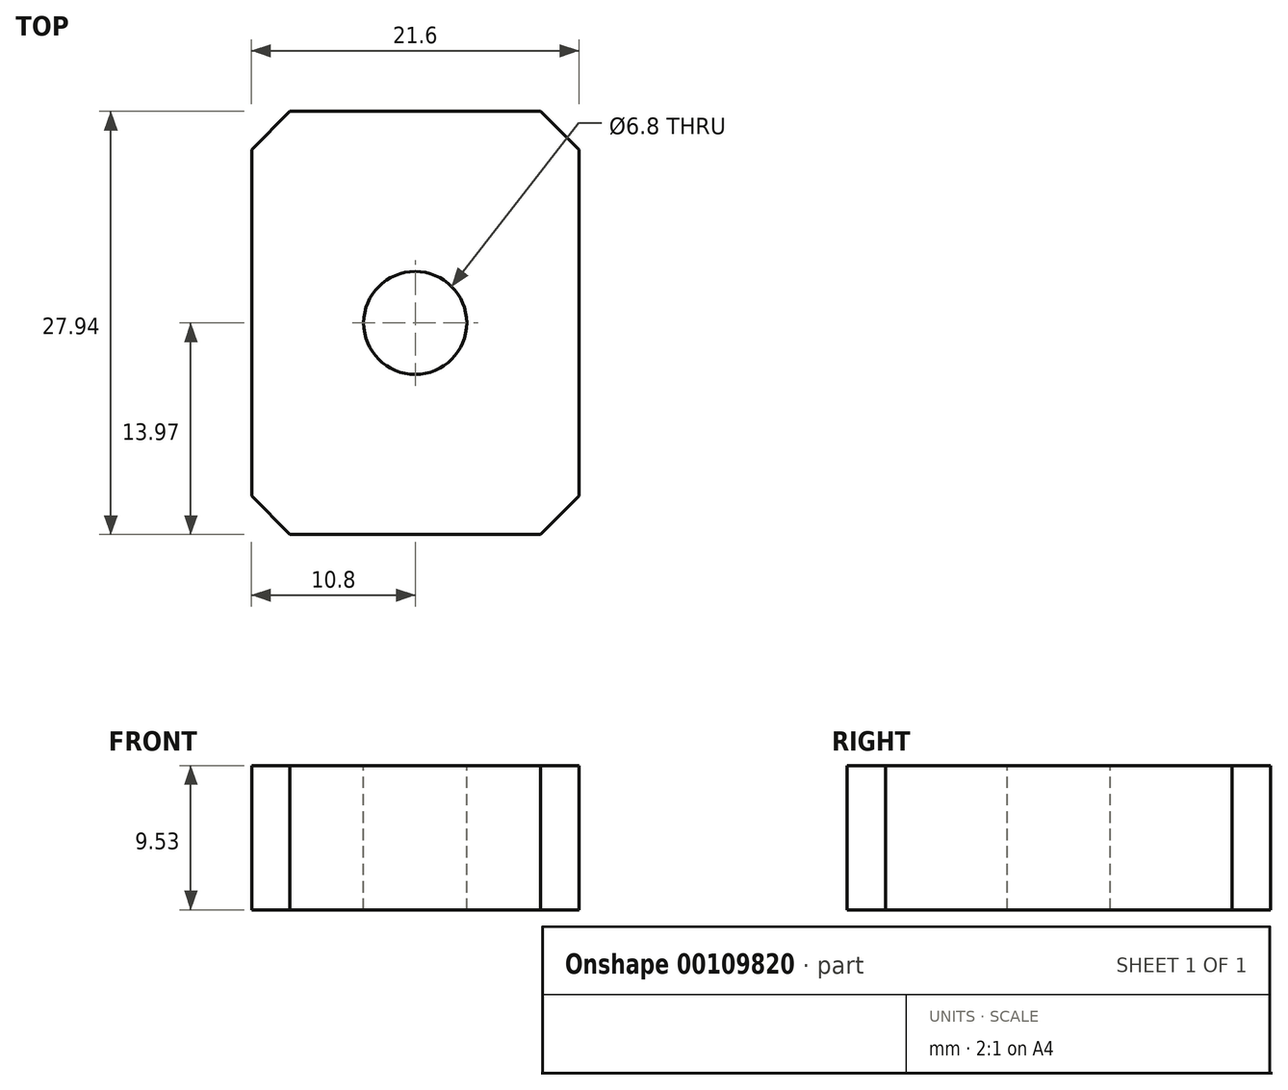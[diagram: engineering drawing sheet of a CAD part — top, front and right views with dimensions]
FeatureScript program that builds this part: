
annotation { "Feature Type Name" : "Feature", "Feature Type Description" : "" }
export const myFeature = defineFeature(function(context is Context, id is Id, definition is map)
    precondition{}
    {
        {
            var Q0;
            Q0=qCreatedBy(makeId("Top.planeOp"),FACE);
            var sketch = newSketch(context, id + "F0", { "sketchPlane" : qUnion([Q0])});
            skLineSegment(sketch, "E0.bottom", {"start": v(10.8, -13.97) * mm, "end": v(-10.8, -13.97) * mm});
            skLineSegment(sketch, "E0.top", {"start": v(10.8, 13.97) * mm, "end": v(-10.8, 13.97) * mm});
            skLineSegment(sketch, "E0.left", {"start": v(10.8, -13.97) * mm, "end": v(10.8, 13.97) * mm});
            skLineSegment(sketch, "E0.right", {"start": v(-10.8, -13.97) * mm, "end": v(-10.8, 13.97) * mm});
            skPoint(sketch, "E0.middle", {"position": v(0, 0) * mm});
            skSolve(sketch);
        }
        {
            var Q0;
            Q0 = qSketchRegion(id + "F0", true);
            extrude(context, id + "F1", {"entities" : qUnion([Q0]), "depth" : 9.52 * mm});
        }
        {
            var Q0;
            Q0=makeQuery(id+"F1.opExtrude","SWEPT_EDGE",EDGE,{"disambiguationData":[OSD([sQuery(id+"F0.wireOp",EDGE,"E0.top"),sQuery(id+"F0.wireOp",EDGE,"E0.right")])]});
            var Q1;
            Q1=makeQuery(id+"F1.opExtrude","SWEPT_EDGE",EDGE,{"disambiguationData":[OSD([sQuery(id+"F0.wireOp",EDGE,"E0.bottom"),sQuery(id+"F0.wireOp",EDGE,"E0.right")])]});
            var Q2;
            Q2=makeQuery(id+"F1.opExtrude","SWEPT_EDGE",EDGE,{"disambiguationData":[OSD([sQuery(id+"F0.wireOp",EDGE,"E0.bottom"),sQuery(id+"F0.wireOp",EDGE,"E0.left")])]});
            var Q3;
            Q3=makeQuery(id+"F1.opExtrude","SWEPT_EDGE",EDGE,{"disambiguationData":[OSD([sQuery(id+"F0.wireOp",EDGE,"E0.top"),sQuery(id+"F0.wireOp",EDGE,"E0.left")])]});
            chamfer(context, id + "F2", {"entities" : qUnion([Q0, Q1, Q2, Q3]), "chamferType" : ChamferType.OFFSET_ANGLE, "width" : 2.54 * mm, "oppositeDirection" : false, "angle" : 45 * degree, "tangentPropagation" : true});
        }
        {
            var Q0;
            Q0=makeQuery(id+"F1.opExtrude","CAP_FACE",FACE,{"disambiguationData":[OSD([sQuery(id+"F0.wireOp",EDGE,"E0.bottom"),sQuery(id+"F0.wireOp",EDGE,"E0.top"),sQuery(id+"F0.wireOp",EDGE,"E0.left"),sQuery(id+"F0.wireOp",EDGE,"E0.right")])],"isStart":false});
            var sketch = newSketch(context, id + "F3", { "sketchPlane" : qUnion([Q0])});
            skCircle(sketch, "E1", {"center": v(0, 0) * mm, "radius": 3.3 * mm});
            skSolve(sketch);
        }
        {
            var Q0;
            Q0 = qSketchRegion(id + "F3", true);
            extrude(context, id + "F4", {"entities" : qUnion([Q0]), "operationType" : NewBodyOperationType.REMOVE, "endBound" : BoundingType.THROUGH_ALL, "oppositeDirection" : true, "depth" : 25.4 * mm});
        }
        {
            var Q0;
            Q0=makeQuery(id+"F1.opExtrude","CAP_FACE",FACE,{"disambiguationData":[OSD([sQuery(id+"F0.wireOp",EDGE,"E0.bottom"),sQuery(id+"F0.wireOp",EDGE,"E0.top"),sQuery(id+"F0.wireOp",EDGE,"E0.left"),sQuery(id+"F0.wireOp",EDGE,"E0.right")])],"isStart":false});
            var sketch = newSketch(context, id + "F5", { "sketchPlane" : qUnion([Q0])});
            skLineSegment(sketch, "E2", {"start": v(0, 13.97) * mm, "end": v(0, -13.97) * mm, "construction": true});
            skLineSegment(sketch, "E3", {"start": v(-10.8, 0) * mm, "end": v(10.8, 0) * mm, "construction": true});
            skPoint(sketch, "E4", {"position": v(0, 0) * mm});
            skSolve(sketch);
        }
        {
            var Q0;
            Q0=sQuery(id+"F5.wireOp",VERTEX,"E4");
            var Q1;
            Q1=makeQuery(id+"F1.opExtrude","SWEPT_BODY",BODY,{"disambiguationData":[OSD([sQuery(id+"F0.wireOp",EDGE,"E0.bottom"),sQuery(id+"F0.wireOp",EDGE,"E0.top"),sQuery(id+"F0.wireOp",EDGE,"E0.left"),sQuery(id+"F0.wireOp",EDGE,"E0.right")])]});
            hole(context, id + "F6", {"style" : HoleStyle.SIMPLE, "endStyle" : HoleEndStyle.THROUGH, "standardTappedOrClearance" : lookupTablePath({ "standard" : "ISO", "engagement" : "75%", "pitch" : "1.25 mm", "size" : "M8", "type" : "Tapped" }), "standardBlindInLast" : lookupTablePath({ "standard" : "ISO", "engagement" : "75%", "pitch" : "1.25 mm", "size" : "M8", "type" : "Tapped" }), "holeDiameter" : 6.8 * mm, "locations" : qUnion([Q0]), "scope" : qUnion([Q1]), "isTappedThrough" : true, "majorDiameter" : 8 * mm, "showTappedDepth" : true});
        }
    });
